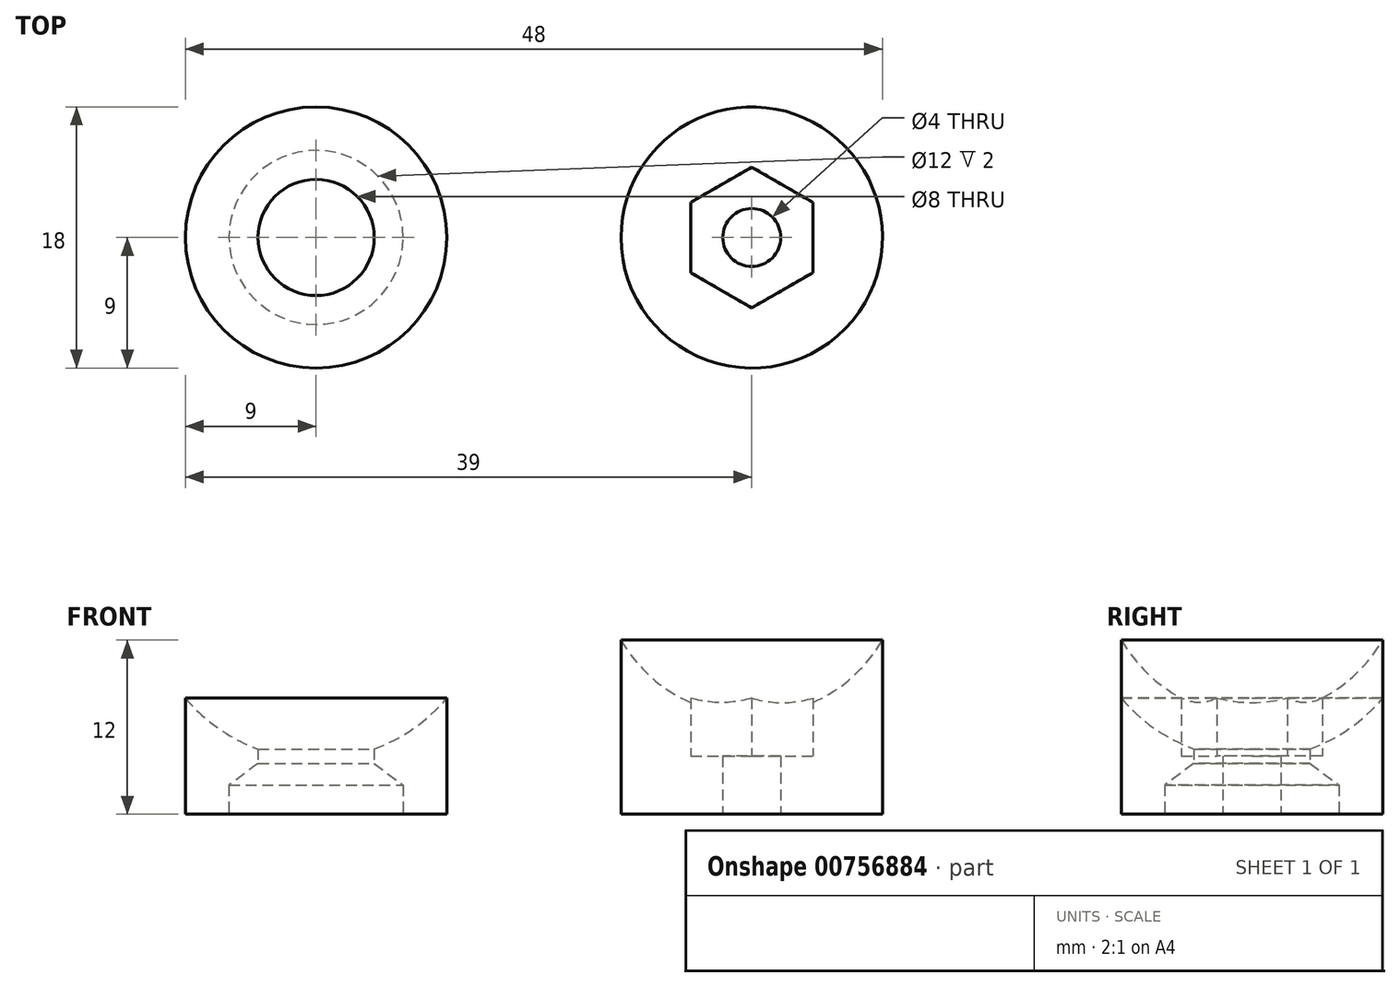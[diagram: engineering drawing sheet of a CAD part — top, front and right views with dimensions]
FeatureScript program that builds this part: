
annotation { "Feature Type Name" : "Feature", "Feature Type Description" : "" }
export const myFeature = defineFeature(function(context is Context, id is Id, definition is map)
    precondition{}
    {
        {
            var Q0;
            Q0=qCreatedBy(makeId("Front.planeOp"),FACE);
            var sketch = newSketch(context, id + "F0", { "sketchPlane" : qUnion([Q0])});
            skLineSegment(sketch, "E0", {"start": v(6, 0) * mm, "end": v(6, 2) * mm});
            skLineSegment(sketch, "E1", {"start": v(6, 2) * mm, "end": v(4, 3.5) * mm});
            skLineSegment(sketch, "E2", {"start": v(4, 3.5) * mm, "end": v(4, 4.5) * mm});
            skLineSegment(sketch, "E3", {"start": v(6, 0) * mm, "end": v(9, 0) * mm});
            skLineSegment(sketch, "E4", {"start": v(9, 0) * mm, "end": v(9, 8) * mm});
            skArc(sketch, "E5", {"start": v(4, 4.5) * mm, "mid": v(6.73, 5.92) * mm, "end": v(9, 8) * mm});
            skSolve(sketch);
        }
        {
            var Q0;
            Q0=qCreatedBy(makeId("Front.planeOp"),FACE);
            var sketch = newSketch(context, id + "F1", { "sketchPlane" : qUnion([Q0])});
            skLineSegment(sketch, "E6", {"start": v(0, 0) * mm, "end": v(0, 17.35) * mm, "construction": true});
            skSolve(sketch);
        }
        {
            var Q0;
            Q0 = qSketchRegion(id + "F0", true);
            var Q1;
            Q1=sQuery(id+"F1.wireOp",EDGE,"E6");
            revolve(context, id + "F2", {"surfaceOperationType" : NewSurfaceOperationType.NEW, "entities" : qUnion([Q0]), "axis" : qUnion([Q1]), "revolveType" : RevolveType.FULL});
        }
        {
            var Q0;
            Q0=qCreatedBy(makeId("Front.planeOp"),FACE);
            var sketch = newSketch(context, id + "F3", { "sketchPlane" : qUnion([Q0])});
            skLineSegment(sketch, "E7", {"start": v(30, 0) * mm, "end": v(30, 30) * mm, "construction": true});
            skSolve(sketch);
        }
        {
            var Q0;
            Q0=qCreatedBy(makeId("Front.planeOp"),FACE);
            var sketch = newSketch(context, id + "F4", { "sketchPlane" : qUnion([Q0])});
            skLineSegment(sketch, "E8", {"start": v(32, 0) * mm, "end": v(39, 0) * mm});
            skLineSegment(sketch, "E9", {"start": v(39, 0) * mm, "end": v(39, 12) * mm});
            skLineSegment(sketch, "E10", {"start": v(32, 0) * mm, "end": v(32, 7) * mm});
            skArc(sketch, "E11", {"start": v(32, 7) * mm, "mid": v(36.04, 8.74) * mm, "end": v(39, 12) * mm});
            skSolve(sketch);
        }
        {
            var Q0;
            Q0 = qSketchRegion(id + "F4", true);
            var Q1;
            Q1=sQuery(id+"F3.wireOp",EDGE,"E7");
            revolve(context, id + "F5", {"surfaceOperationType" : NewSurfaceOperationType.NEW, "entities" : qUnion([Q0]), "axis" : qUnion([Q1]), "revolveType" : RevolveType.FULL});
        }
        {
            var Q0;
            Q0=qCreatedBy(makeId("Top.planeOp"),FACE);
            var sketch = newSketch(context, id + "F6", { "sketchPlane" : qUnion([Q0])});
            skLineSegment(sketch, "E12", {"start": v(30, 15) * mm, "end": v(30, -15) * mm, "construction": true});
            skCircle(sketch, "E13.cCircle", {"center": v(30, 0) * mm, "radius": 4.2 * mm, "construction": true});
            skLineSegment(sketch, "E13.0", {"start": v(34.2, 2.42) * mm, "end": v(34.2, -2.42) * mm});
            skLineSegment(sketch, "E13.1", {"start": v(34.2, -2.42) * mm, "end": v(30, -4.85) * mm});
            skLineSegment(sketch, "E13.2", {"start": v(30, -4.85) * mm, "end": v(25.8, -2.42) * mm});
            skLineSegment(sketch, "E13.3", {"start": v(25.8, -2.42) * mm, "end": v(25.8, 2.42) * mm});
            skLineSegment(sketch, "E13.4", {"start": v(25.8, 2.42) * mm, "end": v(30, 4.85) * mm});
            skLineSegment(sketch, "E13.5", {"start": v(30, 4.85) * mm, "end": v(34.2, 2.42) * mm});
            skPoint(sketch, "E13.0.midPoint", {"position": v(34.2, 0) * mm});
            skSolve(sketch);
        }
        {
            var Q0;
            Q0 = qSketchRegion(id + "F6", true);
            extrude(context, id + "F7", {"entities" : qUnion([Q0]), "depth" : 5 * mm, "offsetDistance" : 25 * mm});
        }
        {
            var Q0;
            Q0=makeQuery(id+"F7.opExtrude","SWEPT_BODY",BODY,{"disambiguationData":[OSD([sQuery(id+"F6.wireOp",EDGE,"E13.0"),sQuery(id+"F6.wireOp",EDGE,"E13.1"),sQuery(id+"F6.wireOp",EDGE,"E13.2"),sQuery(id+"F6.wireOp",EDGE,"E13.3"),sQuery(id+"F6.wireOp",EDGE,"E13.4"),sQuery(id+"F6.wireOp",EDGE,"E13.5")])]});
            transform(context, id + "F8", {"entities" : qUnion([Q0]), "transformType" : TransformType.TRANSLATION_3D, "dx" : 0 * mm, "dy" : 0 * mm, "dz" : 4 * mm, "makeCopy" : false});
        }
        {
            var Q0;
            Q0=makeQuery(id+"F7.opExtrude","SWEPT_BODY",BODY,{"disambiguationData":[OSD([sQuery(id+"F6.wireOp",EDGE,"E13.0"),sQuery(id+"F6.wireOp",EDGE,"E13.1"),sQuery(id+"F6.wireOp",EDGE,"E13.2"),sQuery(id+"F6.wireOp",EDGE,"E13.3"),sQuery(id+"F6.wireOp",EDGE,"E13.4"),sQuery(id+"F6.wireOp",EDGE,"E13.5")])]});
            var Q1;
            Q1=makeQuery(id+"F5.opRevolve","SWEPT_BODY",BODY,{"disambiguationData":[OSD([sQuery(id+"F4.wireOp",EDGE,"E8"),sQuery(id+"F4.wireOp",EDGE,"E9"),sQuery(id+"F4.wireOp",EDGE,"E10"),sQuery(id+"F4.wireOp",EDGE,"E11")])]});
            booleanBodies(context, id + "F9", {"operationType" : BooleanOperationType.SUBTRACTION, "tools" : qUnion([Q0]), "targets" : qUnion([Q1])});
        }
    });
